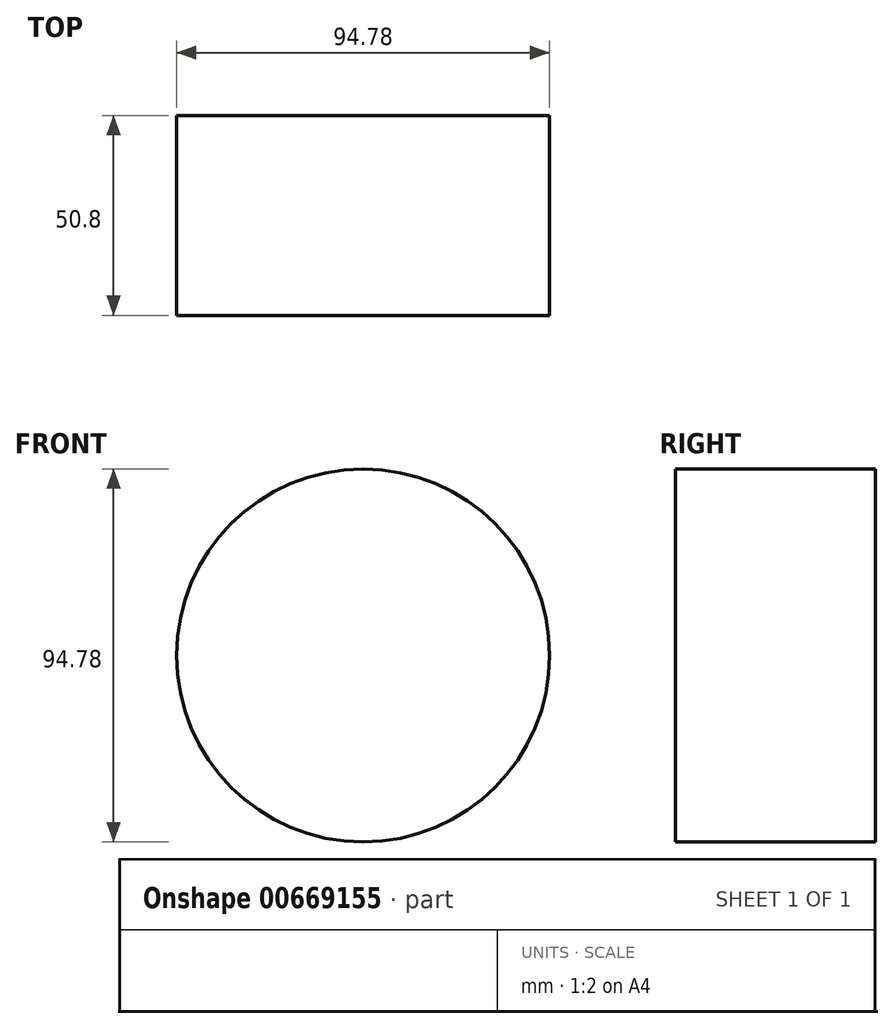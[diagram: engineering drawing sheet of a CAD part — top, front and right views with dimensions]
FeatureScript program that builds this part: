
annotation { "Feature Type Name" : "Feature", "Feature Type Description" : "" }
export const myFeature = defineFeature(function(context is Context, id is Id, definition is map)
    precondition{}
    {
        {
            var Q0;
            Q0=qCreatedBy(makeId("Front.planeOp"),FACE);
            var sketch = newSketch(context, id + "F0", { "sketchPlane" : qUnion([Q0])});
            skCircle(sketch, "E0", {"center": v(0, 0) * mm, "radius": 47.39 * mm});
            skSolve(sketch);
        }
        {
            var Q0;
            Q0=makeQuery(id+"F0.imprint","IMPRINT",FACE,{"disambiguationData":[TD([[makeQuery(id+"F0.imprint","IMPRINT",EDGE,{"derivedFrom":sQuery(id+"F0.wireOp",EDGE,"E0")}),1.0]])]});
            extrude(context, id + "F1", {"entities" : qUnion([Q0]), "depth" : 50.8 * mm, "offsetDistance" : 25.4 * mm});
        }
    });
